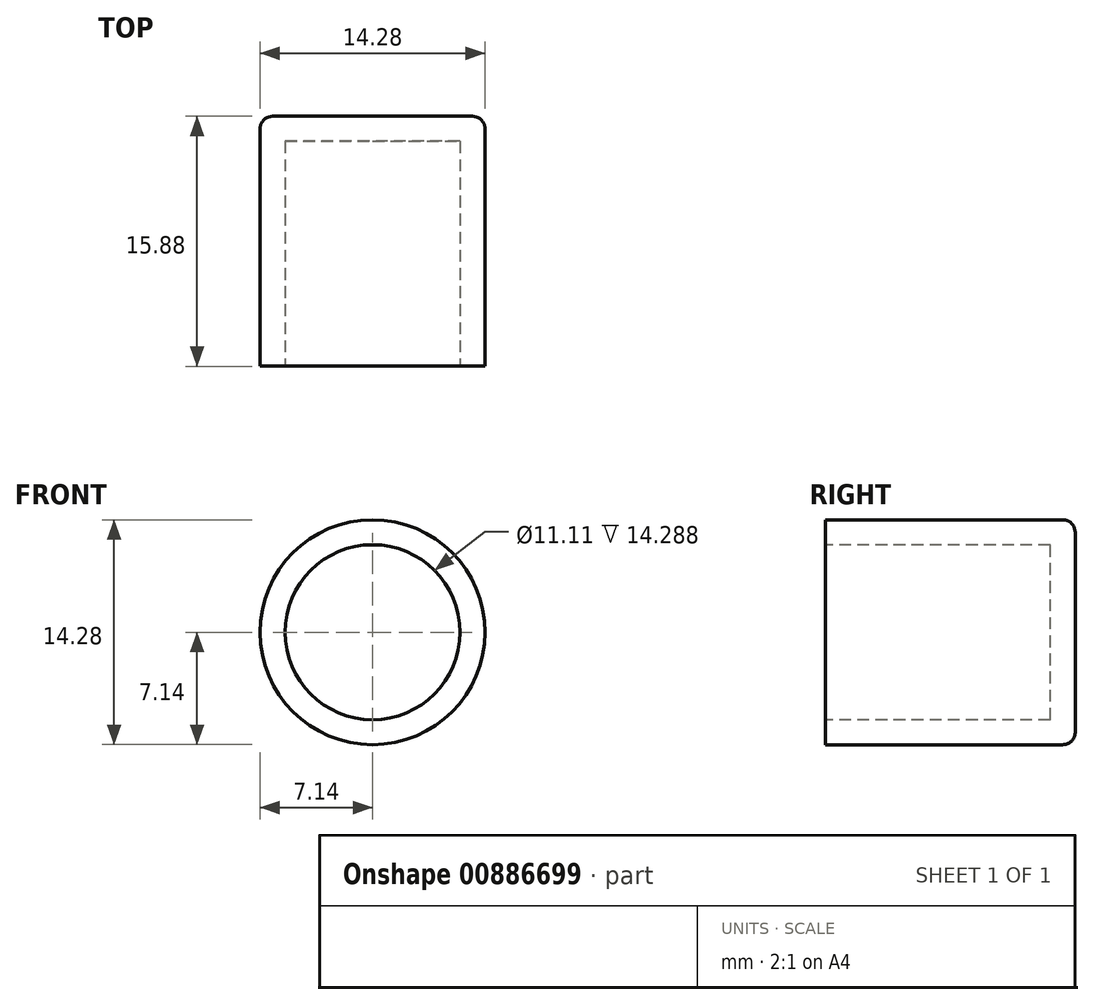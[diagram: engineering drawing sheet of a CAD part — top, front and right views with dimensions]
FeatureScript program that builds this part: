
annotation { "Feature Type Name" : "Feature", "Feature Type Description" : "" }
export const myFeature = defineFeature(function(context is Context, id is Id, definition is map)
    precondition{}
    {
        {
            var Q0;
            Q0=qCreatedBy(makeId("Top.planeOp"),FACE);
            var sketch = newSketch(context, id + "F0", { "sketchPlane" : qUnion([Q0])});
            skLineSegment(sketch, "E0.bottom", {"start": v(-7.14, -7.94) * mm, "end": v(-5.56, -7.94) * mm});
            skLineSegment(sketch, "E0.top", {"start": v(-6.35, 7.94) * mm, "end": v(0, 7.94) * mm});
            skLineSegment(sketch, "E0.left", {"start": v(-7.14, -7.94) * mm, "end": v(-7.14, 7.14) * mm});
            skPoint(sketch, "E0.middle", {"position": v(0, 0) * mm});
            skLineSegment(sketch, "E1.0", {"start": v(-5.56, -7.94) * mm, "end": v(-5.56, 6.35) * mm});
            skLineSegment(sketch, "E2.0", {"start": v(-5.56, 6.35) * mm, "end": v(0, 6.35) * mm});
            skLineSegment(sketch, "E3", {"start": v(0, 6.35) * mm, "end": v(0, 7.94) * mm});
            skPoint(sketch, "E3.endSnap0", {"position": v(0, 6.35) * mm});
            skPoint(sketch, "E4.visualSharp", {"position": v(-7.14, 7.94) * mm});
            skArc(sketch, "E4.filletArc", {"start": v(-6.35, 7.94) * mm, "mid": v(-6.91, 7.7) * mm, "end": v(-7.14, 7.14) * mm});
            skSolve(sketch);
        }
        {
            var Q0;
            Q0=qSketchRegion(id+"F0",true);
            var Q1;
            Q1=sQuery(id+"F0.wireOp",EDGE,"E3");
            revolve(context, id + "F1", {"surfaceOperationType" : NewSurfaceOperationType.NEW, "entities" : qUnion([Q0]), "axis" : qUnion([Q1]), "revolveType" : RevolveType.FULL});
        }
    });
